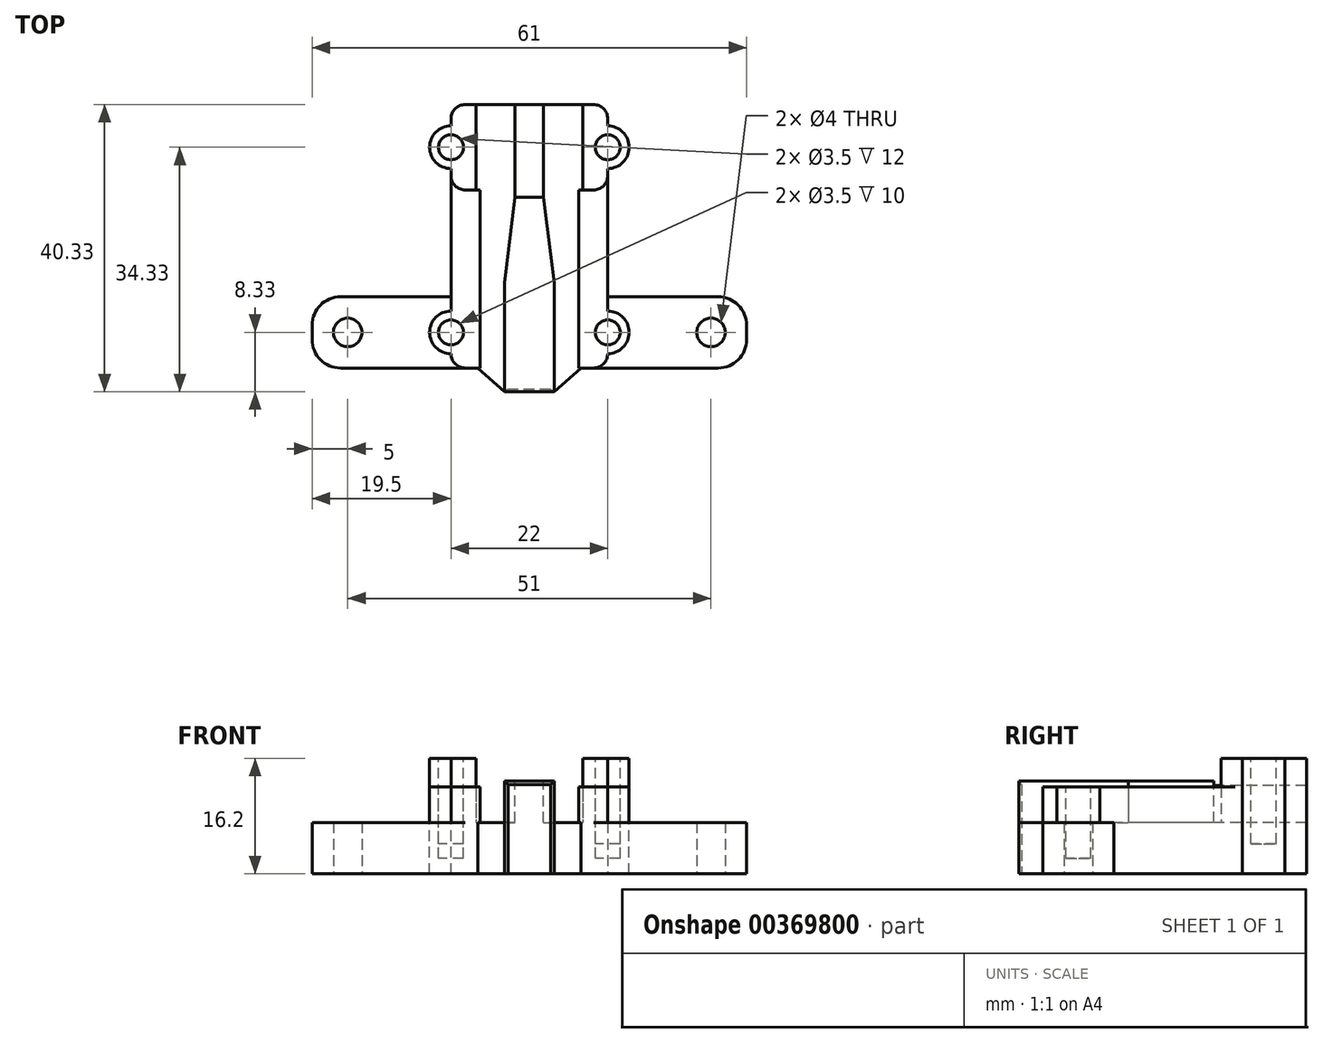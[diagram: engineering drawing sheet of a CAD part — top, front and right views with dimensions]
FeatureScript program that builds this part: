
annotation { "Feature Type Name" : "Feature", "Feature Type Description" : "" }
export const myFeature = defineFeature(function(context is Context, id is Id, definition is map)
    precondition{}
    {
        {
            var Q0;
            Q0=qCreatedBy(makeId("Top.planeOp"),FACE);
            var sketch = newSketch(context, id + "F0", { "sketchPlane" : qUnion([Q0])});
            skLineSegment(sketch, "E0.bottom", {"start": v(0, 0) * mm, "end": v(7, 0) * mm});
            skLineSegment(sketch, "E0.top", {"start": v(0, 15) * mm, "end": v(7, 15) * mm});
            skLineSegment(sketch, "E0.left", {"start": v(0, 0) * mm, "end": v(0, 15) * mm});
            skLineSegment(sketch, "E0.right", {"start": v(7, 0) * mm, "end": v(7, 15) * mm});
            skSolve(sketch);
        }
        {
            var Q0;
            Q0 = qSketchRegion(id + "F0", true);
            extrude(context, id + "F1", {"entities" : qUnion([Q0]), "depth" : 13 * mm});
        }
        {
            var Q0;
            Q0=makeQuery(id+"F1.opExtrude","SWEPT_FACE",FACE,{"disambiguationData":[OSD([sQuery(id+"F0.wireOp",EDGE,"E0.left")])]});
            var sketch = newSketch(context, id + "F2", { "sketchPlane" : qUnion([Q0])});
            skLineSegment(sketch, "E1", {"start": v(0, 13) * mm, "end": v(0.33, 13) * mm});
            skLineSegment(sketch, "E2", {"start": v(0.33, 13) * mm, "end": v(0, 12.5) * mm});
            skLineSegment(sketch, "E3", {"start": v(0, 12.5) * mm, "end": v(0, 13) * mm});
            skSolve(sketch);
        }
        {
            var Q0;
            Q0 = qSketchRegion(id + "F2", true);
            var Q1;
            Q1=makeQuery(id+"F1.opExtrude","SWEPT_FACE",FACE,{"disambiguationData":[OSD([sQuery(id+"F0.wireOp",EDGE,"E0.right")])]});
            extrude(context, id + "F3", {"entities" : qUnion([Q0]), "operationType" : NewBodyOperationType.ADD, "endBound" : BoundingType.UP_TO_SURFACE, "oppositeDirection" : true, "endBoundEntityFace" : qUnion([Q1]), "depth" : 25 * mm});
        }
        {
            var Q0;
            Q0=makeQuery(id+"F1.opExtrude","CAP_FACE",FACE,{"disambiguationData":[OSD([sQuery(id+"F0.wireOp",EDGE,"E0.bottom"),sQuery(id+"F0.wireOp",EDGE,"E0.top"),sQuery(id+"F0.wireOp",EDGE,"E0.left"),sQuery(id+"F0.wireOp",EDGE,"E0.right")])],"isStart":true});
            var sketch = newSketch(context, id + "F4", { "sketchPlane" : qUnion([Q0])});
            skLineSegment(sketch, "E4", {"start": v(0, 0) * mm, "end": v(0, 0.33) * mm});
            skLineSegment(sketch, "E5", {"start": v(0, 0.33) * mm, "end": v(0.5, 0) * mm});
            skLineSegment(sketch, "E6", {"start": v(0.5, 0) * mm, "end": v(0, 0) * mm});
            skLineSegment(sketch, "E7", {"start": v(7, 0) * mm, "end": v(7, 0.33) * mm});
            skLineSegment(sketch, "E8", {"start": v(7, 0.33) * mm, "end": v(6.5, 0) * mm});
            skLineSegment(sketch, "E9", {"start": v(6.5, 0) * mm, "end": v(7, 0) * mm});
            skSolve(sketch);
        }
        {
            var Q0;
            Q0 = qSketchRegion(id + "F4", true);
            var Q1;
            Q1=makeQuery(id+"F3.boolean.opBoolean","MERGE",FACE,{"derivedFrom":[makeQuery(id+"F1.opExtrude","CAP_FACE",FACE,{"disambiguationData":[OSD([sQuery(id+"F0.wireOp",EDGE,"E0.bottom"),sQuery(id+"F0.wireOp",EDGE,"E0.top"),sQuery(id+"F0.wireOp",EDGE,"E0.left"),sQuery(id+"F0.wireOp",EDGE,"E0.right")])],"isStart":false}),makeQuery(id+"F3.opExtrude","SWEPT_FACE",FACE,{"disambiguationData":[OSD([sQuery(id+"F2.wireOp",EDGE,"E1")])]})]});
            extrude(context, id + "F5", {"entities" : qUnion([Q0]), "operationType" : NewBodyOperationType.ADD, "endBound" : BoundingType.UP_TO_SURFACE, "oppositeDirection" : true, "endBoundEntityFace" : qUnion([Q1]), "depth" : 25 * mm});
        }
        {
            var Q0;
            Q0=makeQuery(id+"F5.boolean.opBoolean","MERGE",FACE,{"derivedFrom":[makeQuery(id+"F1.opExtrude","CAP_FACE",FACE,{"disambiguationData":[OSD([sQuery(id+"F0.wireOp",EDGE,"E0.bottom"),sQuery(id+"F0.wireOp",EDGE,"E0.top"),sQuery(id+"F0.wireOp",EDGE,"E0.left"),sQuery(id+"F0.wireOp",EDGE,"E0.right")])],"isStart":true}),makeQuery(id+"F5.opExtrude","CAP_FACE",FACE,{"disambiguationData":[OSD([sQuery(id+"F4.wireOp",EDGE,"E4"),sQuery(id+"F4.wireOp",EDGE,"E5"),sQuery(id+"F4.wireOp",EDGE,"E6")])],"isStart":true}),makeQuery(id+"F5.opExtrude","CAP_FACE",FACE,{"disambiguationData":[OSD([sQuery(id+"F4.wireOp",EDGE,"E7"),sQuery(id+"F4.wireOp",EDGE,"E8"),sQuery(id+"F4.wireOp",EDGE,"E9")])],"isStart":true})]});
            var sketch = newSketch(context, id + "F6", { "sketchPlane" : qUnion([Q0])});
            skLineSegment(sketch, "E10.bottom", {"start": v(0, -3) * mm, "end": v(-23, -3) * mm});
            skLineSegment(sketch, "E10.top", {"start": v(0, -13) * mm, "end": v(-23, -13) * mm});
            skLineSegment(sketch, "E10.left", {"start": v(0, -3) * mm, "end": v(0, -13) * mm});
            skLineSegment(sketch, "E10.right", {"start": v(-27, -7) * mm, "end": v(-27, -9) * mm});
            skLineSegment(sketch, "E11.bottom", {"start": v(7, -3) * mm, "end": v(30, -3) * mm});
            skLineSegment(sketch, "E11.top", {"start": v(7, -13) * mm, "end": v(30, -13) * mm});
            skLineSegment(sketch, "E11.left", {"start": v(7, -3) * mm, "end": v(7, -13) * mm});
            skLineSegment(sketch, "E11.right", {"start": v(34, -7) * mm, "end": v(34, -9) * mm});
            skPoint(sketch, "E12.visualSharp", {"position": v(34, -13) * mm});
            skArc(sketch, "E12.filletArc", {"start": v(30, -13) * mm, "mid": v(32.83, -11.83) * mm, "end": v(34, -9) * mm});
            skPoint(sketch, "E13.visualSharp", {"position": v(34, -3) * mm});
            skArc(sketch, "E13.filletArc", {"start": v(34, -7) * mm, "mid": v(32.83, -4.17) * mm, "end": v(30, -3) * mm});
            skPoint(sketch, "E14.visualSharp", {"position": v(-27, -13) * mm});
            skArc(sketch, "E14.filletArc", {"start": v(-27, -9) * mm, "mid": v(-25.83, -11.83) * mm, "end": v(-23, -13) * mm});
            skPoint(sketch, "E15.visualSharp", {"position": v(-27, -3) * mm});
            skArc(sketch, "E15.filletArc", {"start": v(-23, -3) * mm, "mid": v(-25.83, -4.17) * mm, "end": v(-27, -7) * mm});
            skSolve(sketch);
        }
        {
            var Q0;
            Q0 = qSketchRegion(id + "F6", true);
            extrude(context, id + "F7", {"entities" : qUnion([Q0]), "operationType" : NewBodyOperationType.ADD, "oppositeDirection" : true, "depth" : 7.2 * mm});
        }
        {
            var Q0;
            Q0=makeQuery(id+"F7.boolean.opBoolean","MERGE",FACE,{"derivedFrom":[makeQuery(id+"F5.boolean.opBoolean","MERGE",FACE,{"derivedFrom":[makeQuery(id+"F1.opExtrude","CAP_FACE",FACE,{"disambiguationData":[OSD([sQuery(id+"F0.wireOp",EDGE,"E0.bottom"),sQuery(id+"F0.wireOp",EDGE,"E0.top"),sQuery(id+"F0.wireOp",EDGE,"E0.left"),sQuery(id+"F0.wireOp",EDGE,"E0.right")])],"isStart":true}),makeQuery(id+"F5.opExtrude","CAP_FACE",FACE,{"disambiguationData":[OSD([sQuery(id+"F4.wireOp",EDGE,"E4"),sQuery(id+"F4.wireOp",EDGE,"E5"),sQuery(id+"F4.wireOp",EDGE,"E6")])],"isStart":true}),makeQuery(id+"F5.opExtrude","CAP_FACE",FACE,{"disambiguationData":[OSD([sQuery(id+"F4.wireOp",EDGE,"E7"),sQuery(id+"F4.wireOp",EDGE,"E8"),sQuery(id+"F4.wireOp",EDGE,"E9")])],"isStart":true})]}),makeQuery(id+"F7.opExtrude","CAP_FACE",FACE,{"disambiguationData":[OSD([sQuery(id+"F6.wireOp",EDGE,"E10.bottom"),sQuery(id+"F6.wireOp",EDGE,"E10.top"),sQuery(id+"F6.wireOp",EDGE,"E10.left"),sQuery(id+"F6.wireOp",EDGE,"E10.right")])],"isStart":true}),makeQuery(id+"F7.opExtrude","CAP_FACE",FACE,{"disambiguationData":[OSD([sQuery(id+"F6.wireOp",EDGE,"E11.bottom"),sQuery(id+"F6.wireOp",EDGE,"E11.top"),sQuery(id+"F6.wireOp",EDGE,"E11.left"),sQuery(id+"F6.wireOp",EDGE,"E11.right")])],"isStart":true})]});
            var sketch = newSketch(context, id + "F8", { "sketchPlane" : qUnion([Q0])});
            skCircle(sketch, "E16", {"center": v(-22, -8) * mm, "radius": 2 * mm});
            skCircle(sketch, "E17", {"center": v(29, -8) * mm, "radius": 2 * mm});
            skSolve(sketch);
        }
        {
            var Q0;
            Q0 = qSketchRegion(id + "F8", true);
            extrude(context, id + "F9", {"entities" : qUnion([Q0]), "operationType" : NewBodyOperationType.REMOVE, "oppositeDirection" : true, "depth" : 25 * mm});
        }
        {
            var Q0;
            Q0=makeQuery(id+"F1.opExtrude","SWEPT_FACE",FACE,{"disambiguationData":[OSD([sQuery(id+"F0.wireOp",EDGE,"E0.top")])]});
            var sketch = newSketch(context, id + "F10", { "sketchPlane" : qUnion([Q0])});
            skLineSegment(sketch, "E18.bottom", {"start": v(-5.5, 12.4) * mm, "end": v(-1.5, 12.4) * mm});
            skLineSegment(sketch, "E18.top", {"start": v(-5.5, 0) * mm, "end": v(-1.5, 0) * mm});
            skLineSegment(sketch, "E18.left", {"start": v(-5.5, 12.4) * mm, "end": v(-5.5, 0) * mm});
            skLineSegment(sketch, "E18.right", {"start": v(-1.5, 12.4) * mm, "end": v(-1.5, 0) * mm});
            skSolve(sketch);
        }
        {
            var Q0;
            Q0 = qSketchRegion(id + "F10", true);
            extrude(context, id + "F11", {"entities" : qUnion([Q0]), "operationType" : NewBodyOperationType.ADD, "depth" : 25 * mm});
        }
        {
            var Q0;
            Q0=makeQuery(id+"F11.boolean.opBoolean","MERGE",FACE,{"derivedFrom":[makeQuery(id+"F7.boolean.opBoolean","MERGE",FACE,{"derivedFrom":[makeQuery(id+"F5.boolean.opBoolean","MERGE",FACE,{"derivedFrom":[makeQuery(id+"F1.opExtrude","CAP_FACE",FACE,{"disambiguationData":[OSD([sQuery(id+"F0.wireOp",EDGE,"E0.bottom"),sQuery(id+"F0.wireOp",EDGE,"E0.top"),sQuery(id+"F0.wireOp",EDGE,"E0.left"),sQuery(id+"F0.wireOp",EDGE,"E0.right")])],"isStart":true}),makeQuery(id+"F5.opExtrude","CAP_FACE",FACE,{"disambiguationData":[OSD([sQuery(id+"F4.wireOp",EDGE,"E4"),sQuery(id+"F4.wireOp",EDGE,"E5"),sQuery(id+"F4.wireOp",EDGE,"E6")])],"isStart":true}),makeQuery(id+"F5.opExtrude","CAP_FACE",FACE,{"disambiguationData":[OSD([sQuery(id+"F4.wireOp",EDGE,"E7"),sQuery(id+"F4.wireOp",EDGE,"E8"),sQuery(id+"F4.wireOp",EDGE,"E9")])],"isStart":true})]}),makeQuery(id+"F7.opExtrude","CAP_FACE",FACE,{"disambiguationData":[OSD([sQuery(id+"F6.wireOp",EDGE,"E10.bottom"),sQuery(id+"F6.wireOp",EDGE,"E10.top"),sQuery(id+"F6.wireOp",EDGE,"E10.left"),sQuery(id+"F6.wireOp",EDGE,"E10.right"),sQuery(id+"F6.wireOp",EDGE,"E14.filletArc"),sQuery(id+"F6.wireOp",EDGE,"E15.filletArc")])],"isStart":true}),makeQuery(id+"F7.opExtrude","CAP_FACE",FACE,{"disambiguationData":[OSD([sQuery(id+"F6.wireOp",EDGE,"E11.bottom"),sQuery(id+"F6.wireOp",EDGE,"E11.top"),sQuery(id+"F6.wireOp",EDGE,"E11.left"),sQuery(id+"F6.wireOp",EDGE,"E11.right"),sQuery(id+"F6.wireOp",EDGE,"E12.filletArc"),sQuery(id+"F6.wireOp",EDGE,"E13.filletArc")])],"isStart":true})]}),makeQuery(id+"F11.opExtrude","SWEPT_FACE",FACE,{"disambiguationData":[OSD([sQuery(id+"F10.wireOp",EDGE,"E18.top")])]})]});
            var sketch = newSketch(context, id + "F12", { "sketchPlane" : qUnion([Q0])});
            skLineSegment(sketch, "E19.bottom", {"start": v(-7.5, -15) * mm, "end": v(14.5, -15) * mm});
            skLineSegment(sketch, "E19.top", {"start": v(-7.5, -40) * mm, "end": v(14.5, -40) * mm});
            skLineSegment(sketch, "E19.left", {"start": v(-7.5, -15) * mm, "end": v(-7.5, -40) * mm});
            skLineSegment(sketch, "E19.right", {"start": v(14.5, -15) * mm, "end": v(14.5, -40) * mm});
            skSolve(sketch);
        }
        {
            var Q0;
            Q0 = qSketchRegion(id + "F12", true);
            extrude(context, id + "F13", {"entities" : qUnion([Q0]), "operationType" : NewBodyOperationType.ADD, "oppositeDirection" : true, "depth" : 7.2 * mm});
        }
        {
            var Q0;
            Q0=makeQuery(id+"F7.opExtrude","SWEPT_FACE",FACE,{"disambiguationData":[OSD([sQuery(id+"F6.wireOp",EDGE,"E11.top")])]});
            var sketch = newSketch(context, id + "F14", { "sketchPlane" : qUnion([Q0])});
            skLineSegment(sketch, "E20.bottom", {"start": v(-7, 7.2) * mm, "end": v(-14.5, 7.2) * mm});
            skLineSegment(sketch, "E20.top", {"start": v(-7, 0) * mm, "end": v(-14.5, 0) * mm});
            skLineSegment(sketch, "E20.left", {"start": v(-7, 7.2) * mm, "end": v(-7, 0) * mm});
            skLineSegment(sketch, "E20.right", {"start": v(-14.5, 7.2) * mm, "end": v(-14.5, 0) * mm});
            skLineSegment(sketch, "E21.bottom", {"start": v(0, 0) * mm, "end": v(7.5, 0) * mm});
            skLineSegment(sketch, "E21.top", {"start": v(0, 7.2) * mm, "end": v(7.5, 7.2) * mm});
            skLineSegment(sketch, "E21.left", {"start": v(0, 0) * mm, "end": v(0, 7.2) * mm});
            skLineSegment(sketch, "E21.right", {"start": v(7.5, 0) * mm, "end": v(7.5, 7.2) * mm});
            skSolve(sketch);
        }
        {
            var Q0;
            Q0 = qSketchRegion(id + "F14", true);
            extrude(context, id + "F15", {"entities" : qUnion([Q0]), "operationType" : NewBodyOperationType.ADD, "endBound" : BoundingType.UP_TO_NEXT, "depth" : 25 * mm});
        }
        {
            var Q0;
            Q0=makeQuery(id+"F11.opExtrude","SWEPT_FACE",FACE,{"disambiguationData":[OSD([sQuery(id+"F10.wireOp",EDGE,"E18.bottom")])]});
            var sketch = newSketch(context, id + "F16", { "sketchPlane" : qUnion([Q0])});
            skLineSegment(sketch, "E22.bottom", {"start": v(7, 15) * mm, "end": v(0, 15) * mm});
            skLineSegment(sketch, "E22.top", {"start": v(5.5, 27) * mm, "end": v(1.5, 27) * mm});
            skLineSegment(sketch, "E23", {"start": v(7, 15) * mm, "end": v(5.5, 27) * mm});
            skLineSegment(sketch, "E24", {"start": v(0, 15) * mm, "end": v(1.5, 27) * mm});
            skPoint(sketch, "E22.right.end.orphan", {"position": v(0, 27) * mm});
            skSolve(sketch);
        }
        {
            var Q0;
            Q0 = qSketchRegion(id + "F16", true);
            extrude(context, id + "F17", {"entities" : qUnion([Q0]), "operationType" : NewBodyOperationType.ADD, "oppositeDirection" : true, "depth" : 6 * mm, "hasSecondDirection" : true, "secondDirectionOppositeDirection" : false, "secondDirectionDepth" : .6 * mm});
        }
        {
            var Q0;
            {var subQ1=sQuery(id+"F12.wireOp",EDGE,"E19.bottom");var subQ2=sQuery(id+"F12.wireOp",EDGE,"E19.top");var subQ3=sQuery(id+"F12.wireOp",EDGE,"E19.left");Q0=makeQuery(id+"F13.boolean.opBoolean","SPLIT",FACE,{"disambiguationData":[TD([makeQuery(id+"F1.opExtrude","SWEPT_FACE",FACE,{"disambiguationData":[OSD([sQuery(id+"F0.wireOp",EDGE,"E0.left")])]})])],"derivedFrom":makeQuery(id+"F13.opExtrude","CAP_FACE",FACE,{"disambiguationData":[OSD([subQ1,subQ2,subQ3,sQuery(id+"F12.wireOp",EDGE,"E19.right")])],"isStart":false})});}
            var sketch = newSketch(context, id + "F18", { "sketchPlane" : qUnion([Q0])});
            skLineSegment(sketch, "E25.bottom", {"start": v(-7.5, 40) * mm, "end": v(-4, 40) * mm});
            skLineSegment(sketch, "E25.top", {"start": v(-7.5, 28) * mm, "end": v(-4, 28) * mm});
            skLineSegment(sketch, "E25.left", {"start": v(-7.5, 40) * mm, "end": v(-7.5, 28) * mm});
            skLineSegment(sketch, "E25.right", {"start": v(-4, 40) * mm, "end": v(-4, 28) * mm});
            skSolve(sketch);
        }
        {
            var Q0;
            Q0 = qSketchRegion(id + "F18", true);
            extrude(context, id + "F19", {"entities" : qUnion([Q0]), "operationType" : NewBodyOperationType.ADD, "depth" : 9 * mm});
        }
        {
            var Q0;
            {var subQ0=sQuery(id+"F0.wireOp",EDGE,"E0.right");var subQ2=sQuery(id+"F12.wireOp",EDGE,"E19.bottom");var subQ3=sQuery(id+"F12.wireOp",EDGE,"E19.top");var subQ4=sQuery(id+"F12.wireOp",EDGE,"E19.right");Q0=makeQuery(id+"F13.boolean.opBoolean","SPLIT",FACE,{"disambiguationData":[TD([makeQuery(id+"F1.opExtrude","SWEPT_FACE",FACE,{"disambiguationData":[OSD([subQ0])]})])],"derivedFrom":makeQuery(id+"F13.opExtrude","CAP_FACE",FACE,{"disambiguationData":[OSD([subQ2,subQ3,sQuery(id+"F12.wireOp",EDGE,"E19.left"),subQ4])],"isStart":false})});}
            var sketch = newSketch(context, id + "F20", { "sketchPlane" : qUnion([Q0])});
            skLineSegment(sketch, "E26.bottom", {"start": v(14.5, 40) * mm, "end": v(11, 40) * mm});
            skLineSegment(sketch, "E26.top", {"start": v(14.5, 28) * mm, "end": v(11, 28) * mm});
            skLineSegment(sketch, "E26.left", {"start": v(14.5, 40) * mm, "end": v(14.5, 28) * mm});
            skLineSegment(sketch, "E26.right", {"start": v(11, 40) * mm, "end": v(11, 28) * mm});
            skSolve(sketch);
        }
        {
            var Q0;
            Q0 = qSketchRegion(id + "F20", true);
            extrude(context, id + "F21", {"entities" : qUnion([Q0]), "operationType" : NewBodyOperationType.ADD, "depth" : 9 * mm});
        }
        {
            var Q0;
            Q0=makeQuery(id+"F21.opExtrude","CAP_FACE",FACE,{"disambiguationData":[OSD([sQuery(id+"F20.wireOp",EDGE,"E26.bottom"),sQuery(id+"F20.wireOp",EDGE,"E26.top"),sQuery(id+"F20.wireOp",EDGE,"E26.left"),sQuery(id+"F20.wireOp",EDGE,"E26.right")])],"isStart":false});
            var sketch = newSketch(context, id + "F22", { "sketchPlane" : qUnion([Q0])});
            skCircle(sketch, "E27", {"center": v(14.5, 34) * mm, "radius": 3 * mm});
            skSolve(sketch);
        }
        {
            var Q0;
            Q0 = qSketchRegion(id + "F22", true);
            var Q1;
            Q1=makeQuery(id+"F15.boolean.opBoolean","MERGE",FACE,{"derivedFrom":[makeQuery(id+"F13.boolean.opBoolean","MERGE",FACE,{"derivedFrom":[makeQuery(id+"F11.boolean.opBoolean","MERGE",FACE,{"derivedFrom":[makeQuery(id+"F7.boolean.opBoolean","MERGE",FACE,{"derivedFrom":[makeQuery(id+"F5.boolean.opBoolean","MERGE",FACE,{"derivedFrom":[makeQuery(id+"F1.opExtrude","CAP_FACE",FACE,{"disambiguationData":[OSD([sQuery(id+"F0.wireOp",EDGE,"E0.bottom"),sQuery(id+"F0.wireOp",EDGE,"E0.top"),sQuery(id+"F0.wireOp",EDGE,"E0.left"),sQuery(id+"F0.wireOp",EDGE,"E0.right")])],"isStart":true}),makeQuery(id+"F5.opExtrude","CAP_FACE",FACE,{"disambiguationData":[OSD([sQuery(id+"F4.wireOp",EDGE,"E4"),sQuery(id+"F4.wireOp",EDGE,"E5"),sQuery(id+"F4.wireOp",EDGE,"E6")])],"isStart":true}),makeQuery(id+"F5.opExtrude","CAP_FACE",FACE,{"disambiguationData":[OSD([sQuery(id+"F4.wireOp",EDGE,"E7"),sQuery(id+"F4.wireOp",EDGE,"E8"),sQuery(id+"F4.wireOp",EDGE,"E9")])],"isStart":true})]}),makeQuery(id+"F7.opExtrude","CAP_FACE",FACE,{"disambiguationData":[OSD([sQuery(id+"F6.wireOp",EDGE,"E10.bottom"),sQuery(id+"F6.wireOp",EDGE,"E10.top"),sQuery(id+"F6.wireOp",EDGE,"E10.left"),sQuery(id+"F6.wireOp",EDGE,"E10.right"),sQuery(id+"F6.wireOp",EDGE,"E14.filletArc"),sQuery(id+"F6.wireOp",EDGE,"E15.filletArc")])],"isStart":true}),makeQuery(id+"F7.opExtrude","CAP_FACE",FACE,{"disambiguationData":[OSD([sQuery(id+"F6.wireOp",EDGE,"E11.bottom"),sQuery(id+"F6.wireOp",EDGE,"E11.top"),sQuery(id+"F6.wireOp",EDGE,"E11.left"),sQuery(id+"F6.wireOp",EDGE,"E11.right"),sQuery(id+"F6.wireOp",EDGE,"E12.filletArc"),sQuery(id+"F6.wireOp",EDGE,"E13.filletArc")])],"isStart":true})]}),makeQuery(id+"F11.opExtrude","SWEPT_FACE",FACE,{"disambiguationData":[OSD([sQuery(id+"F10.wireOp",EDGE,"E18.top")])]})]}),makeQuery(id+"F13.opExtrude","CAP_FACE",FACE,{"disambiguationData":[OSD([sQuery(id+"F12.wireOp",EDGE,"E19.bottom"),sQuery(id+"F12.wireOp",EDGE,"E19.top"),sQuery(id+"F12.wireOp",EDGE,"E19.left"),sQuery(id+"F12.wireOp",EDGE,"E19.right")])],"isStart":true})]}),makeQuery(id+"F15.opExtrude","SWEPT_FACE",FACE,{"disambiguationData":[OSD([sQuery(id+"F14.wireOp",EDGE,"E20.top")])]}),makeQuery(id+"F15.opExtrude","SWEPT_FACE",FACE,{"disambiguationData":[OSD([sQuery(id+"F14.wireOp",EDGE,"E21.bottom")])]})]});
            extrude(context, id + "F23", {"entities" : qUnion([Q0]), "operationType" : NewBodyOperationType.ADD, "endBound" : BoundingType.UP_TO_SURFACE, "oppositeDirection" : true, "endBoundEntityFace" : qUnion([Q1]), "depth" : 25 * mm});
        }
        {
            var Q0;
            Q0=makeQuery(id+"F19.opExtrude","CAP_FACE",FACE,{"disambiguationData":[OSD([sQuery(id+"F18.wireOp",EDGE,"E25.bottom"),sQuery(id+"F18.wireOp",EDGE,"E25.top"),sQuery(id+"F18.wireOp",EDGE,"E25.left"),sQuery(id+"F18.wireOp",EDGE,"E25.right")])],"isStart":false});
            var sketch = newSketch(context, id + "F24", { "sketchPlane" : qUnion([Q0])});
            skCircle(sketch, "E28", {"center": v(-7.5, 34) * mm, "radius": 3 * mm});
            skSolve(sketch);
        }
        {
            var Q0;
            Q0 = qSketchRegion(id + "F24", true);
            var Q1;
            Q1=makeQuery(id+"F23.boolean.opBoolean","MERGE",FACE,{"derivedFrom":[makeQuery(id+"F15.boolean.opBoolean","MERGE",FACE,{"derivedFrom":[makeQuery(id+"F13.boolean.opBoolean","MERGE",FACE,{"derivedFrom":[makeQuery(id+"F11.boolean.opBoolean","MERGE",FACE,{"derivedFrom":[makeQuery(id+"F7.boolean.opBoolean","MERGE",FACE,{"derivedFrom":[makeQuery(id+"F5.boolean.opBoolean","MERGE",FACE,{"derivedFrom":[makeQuery(id+"F1.opExtrude","CAP_FACE",FACE,{"disambiguationData":[OSD([sQuery(id+"F0.wireOp",EDGE,"E0.bottom"),sQuery(id+"F0.wireOp",EDGE,"E0.top"),sQuery(id+"F0.wireOp",EDGE,"E0.left"),sQuery(id+"F0.wireOp",EDGE,"E0.right")])],"isStart":true}),makeQuery(id+"F5.opExtrude","CAP_FACE",FACE,{"disambiguationData":[OSD([sQuery(id+"F4.wireOp",EDGE,"E4"),sQuery(id+"F4.wireOp",EDGE,"E5"),sQuery(id+"F4.wireOp",EDGE,"E6")])],"isStart":true}),makeQuery(id+"F5.opExtrude","CAP_FACE",FACE,{"disambiguationData":[OSD([sQuery(id+"F4.wireOp",EDGE,"E7"),sQuery(id+"F4.wireOp",EDGE,"E8"),sQuery(id+"F4.wireOp",EDGE,"E9")])],"isStart":true})]}),makeQuery(id+"F7.opExtrude","CAP_FACE",FACE,{"disambiguationData":[OSD([sQuery(id+"F6.wireOp",EDGE,"E10.bottom"),sQuery(id+"F6.wireOp",EDGE,"E10.top"),sQuery(id+"F6.wireOp",EDGE,"E10.left"),sQuery(id+"F6.wireOp",EDGE,"E10.right"),sQuery(id+"F6.wireOp",EDGE,"E14.filletArc"),sQuery(id+"F6.wireOp",EDGE,"E15.filletArc")])],"isStart":true}),makeQuery(id+"F7.opExtrude","CAP_FACE",FACE,{"disambiguationData":[OSD([sQuery(id+"F6.wireOp",EDGE,"E11.bottom"),sQuery(id+"F6.wireOp",EDGE,"E11.top"),sQuery(id+"F6.wireOp",EDGE,"E11.left"),sQuery(id+"F6.wireOp",EDGE,"E11.right"),sQuery(id+"F6.wireOp",EDGE,"E12.filletArc"),sQuery(id+"F6.wireOp",EDGE,"E13.filletArc")])],"isStart":true})]}),makeQuery(id+"F11.opExtrude","SWEPT_FACE",FACE,{"disambiguationData":[OSD([sQuery(id+"F10.wireOp",EDGE,"E18.top")])]})]}),makeQuery(id+"F13.opExtrude","CAP_FACE",FACE,{"disambiguationData":[OSD([sQuery(id+"F12.wireOp",EDGE,"E19.bottom"),sQuery(id+"F12.wireOp",EDGE,"E19.top"),sQuery(id+"F12.wireOp",EDGE,"E19.left"),sQuery(id+"F12.wireOp",EDGE,"E19.right")])],"isStart":true})]}),makeQuery(id+"F15.opExtrude","SWEPT_FACE",FACE,{"disambiguationData":[OSD([sQuery(id+"F14.wireOp",EDGE,"E20.top")])]}),makeQuery(id+"F15.opExtrude","SWEPT_FACE",FACE,{"disambiguationData":[OSD([sQuery(id+"F14.wireOp",EDGE,"E21.bottom")])]})]}),makeQuery(id+"F23.opExtrude","CAP_FACE",FACE,{"disambiguationData":[OSD([sQuery(id+"F22.wireOp",EDGE,"E27")])],"isStart":false})]});
            extrude(context, id + "F25", {"entities" : qUnion([Q0]), "operationType" : NewBodyOperationType.ADD, "endBound" : BoundingType.UP_TO_SURFACE, "oppositeDirection" : true, "endBoundEntityFace" : qUnion([Q1]), "depth" : 25 * mm});
        }
        {
            var Q0;
            Q0=makeQuery(id+"F25.boolean.opBoolean","MERGE",FACE,{"derivedFrom":[makeQuery(id+"F19.opExtrude","CAP_FACE",FACE,{"disambiguationData":[OSD([sQuery(id+"F18.wireOp",EDGE,"E25.bottom"),sQuery(id+"F18.wireOp",EDGE,"E25.top"),sQuery(id+"F18.wireOp",EDGE,"E25.left"),sQuery(id+"F18.wireOp",EDGE,"E25.right")])],"isStart":false}),makeQuery(id+"F25.opExtrude","CAP_FACE",FACE,{"disambiguationData":[OSD([sQuery(id+"F24.wireOp",EDGE,"E28")])],"isStart":true})]});
            var sketch = newSketch(context, id + "F26", { "sketchPlane" : qUnion([Q0])});
            skCircle(sketch, "E29", {"center": v(-7.5, 34) * mm, "radius": 1.75 * mm});
            skSolve(sketch);
        }
        {
            var Q0;
            Q0 = qSketchRegion(id + "F26", true);
            extrude(context, id + "F27", {"entities" : qUnion([Q0]), "operationType" : NewBodyOperationType.REMOVE, "oppositeDirection" : true, "depth" : 12 * mm});
        }
        {
            var Q0;
            Q0=makeQuery(id+"F23.boolean.opBoolean","MERGE",FACE,{"derivedFrom":[makeQuery(id+"F21.opExtrude","CAP_FACE",FACE,{"disambiguationData":[OSD([sQuery(id+"F20.wireOp",EDGE,"E26.bottom"),sQuery(id+"F20.wireOp",EDGE,"E26.top"),sQuery(id+"F20.wireOp",EDGE,"E26.left"),sQuery(id+"F20.wireOp",EDGE,"E26.right")])],"isStart":false}),makeQuery(id+"F23.opExtrude","CAP_FACE",FACE,{"disambiguationData":[OSD([sQuery(id+"F22.wireOp",EDGE,"E27")])],"isStart":true})]});
            var sketch = newSketch(context, id + "F28", { "sketchPlane" : qUnion([Q0])});
            skCircle(sketch, "E30", {"center": v(14.5, 34) * mm, "radius": 1.75 * mm});
            skSolve(sketch);
        }
        {
            var Q0;
            Q0 = qSketchRegion(id + "F28", true);
            extrude(context, id + "F29", {"entities" : qUnion([Q0]), "operationType" : NewBodyOperationType.REMOVE, "oppositeDirection" : true, "depth" : 12 * mm});
        }
        {
            var Q0;
            {var subQ1=sQuery(id+"F12.wireOp",EDGE,"E19.bottom");var subQ2=sQuery(id+"F12.wireOp",EDGE,"E19.top");var subQ3=sQuery(id+"F12.wireOp",EDGE,"E19.left");Q0=makeQuery(id+"F15.boolean.opBoolean","MERGE",FACE,{"derivedFrom":[makeQuery(id+"F7.opExtrude","CAP_FACE",FACE,{"disambiguationData":[OSD([sQuery(id+"F6.wireOp",EDGE,"E10.bottom"),sQuery(id+"F6.wireOp",EDGE,"E10.top"),sQuery(id+"F6.wireOp",EDGE,"E10.left"),sQuery(id+"F6.wireOp",EDGE,"E10.right"),sQuery(id+"F6.wireOp",EDGE,"E14.filletArc"),sQuery(id+"F6.wireOp",EDGE,"E15.filletArc")])],"isStart":false}),makeQuery(id+"F13.boolean.opBoolean","SPLIT",FACE,{"disambiguationData":[TD([makeQuery(id+"F1.opExtrude","SWEPT_FACE",FACE,{"disambiguationData":[OSD([sQuery(id+"F0.wireOp",EDGE,"E0.left")])]})])],"derivedFrom":makeQuery(id+"F13.opExtrude","CAP_FACE",FACE,{"disambiguationData":[OSD([subQ1,subQ2,subQ3,sQuery(id+"F12.wireOp",EDGE,"E19.right")])],"isStart":false})}),makeQuery(id+"F15.opExtrude","SWEPT_FACE",FACE,{"disambiguationData":[OSD([sQuery(id+"F14.wireOp",EDGE,"E21.top")])]})]});}
            var sketch = newSketch(context, id + "F30", { "sketchPlane" : qUnion([Q0])});
            skLineSegment(sketch, "E31.bottom", {"start": v(-7.5, 28) * mm, "end": v(-3.4, 28) * mm});
            skLineSegment(sketch, "E31.top", {"start": v(-7.5, 3) * mm, "end": v(-3.4, 3) * mm});
            skLineSegment(sketch, "E31.left", {"start": v(-7.5, 28) * mm, "end": v(-7.5, 3) * mm});
            skLineSegment(sketch, "E31.right", {"start": v(-3.4, 28) * mm, "end": v(-3.4, 3) * mm});
            skSolve(sketch);
        }
        {
            var Q0;
            Q0 = qSketchRegion(id + "F30", true);
            extrude(context, id + "F31", {"entities" : qUnion([Q0]), "operationType" : NewBodyOperationType.ADD, "depth" : 5 * mm});
        }
        {
            var Q0;
            {var subQ1=sQuery(id+"F12.wireOp",EDGE,"E19.bottom");var subQ2=sQuery(id+"F12.wireOp",EDGE,"E19.top");var subQ3=sQuery(id+"F12.wireOp",EDGE,"E19.right");Q0=makeQuery(id+"F15.boolean.opBoolean","MERGE",FACE,{"derivedFrom":[makeQuery(id+"F7.opExtrude","CAP_FACE",FACE,{"disambiguationData":[OSD([sQuery(id+"F6.wireOp",EDGE,"E11.bottom"),sQuery(id+"F6.wireOp",EDGE,"E11.top"),sQuery(id+"F6.wireOp",EDGE,"E11.left"),sQuery(id+"F6.wireOp",EDGE,"E11.right"),sQuery(id+"F6.wireOp",EDGE,"E12.filletArc"),sQuery(id+"F6.wireOp",EDGE,"E13.filletArc")])],"isStart":false}),makeQuery(id+"F13.boolean.opBoolean","SPLIT",FACE,{"disambiguationData":[TD([makeQuery(id+"F1.opExtrude","SWEPT_FACE",FACE,{"disambiguationData":[OSD([sQuery(id+"F0.wireOp",EDGE,"E0.right")])]})])],"derivedFrom":makeQuery(id+"F13.opExtrude","CAP_FACE",FACE,{"disambiguationData":[OSD([subQ1,subQ2,sQuery(id+"F12.wireOp",EDGE,"E19.left"),subQ3])],"isStart":false})}),makeQuery(id+"F15.opExtrude","SWEPT_FACE",FACE,{"disambiguationData":[OSD([sQuery(id+"F14.wireOp",EDGE,"E20.bottom")])]})]});}
            var sketch = newSketch(context, id + "F32", { "sketchPlane" : qUnion([Q0])});
            skLineSegment(sketch, "E32.bottom", {"start": v(14.5, 28) * mm, "end": v(10.4, 28) * mm});
            skLineSegment(sketch, "E32.top", {"start": v(14.5, 3) * mm, "end": v(10.4, 3) * mm});
            skLineSegment(sketch, "E32.left", {"start": v(14.5, 28) * mm, "end": v(14.5, 3) * mm});
            skLineSegment(sketch, "E32.right", {"start": v(10.4, 28) * mm, "end": v(10.4, 3) * mm});
            skSolve(sketch);
        }
        {
            var Q0;
            Q0 = qSketchRegion(id + "F32", true);
            extrude(context, id + "F33", {"entities" : qUnion([Q0]), "operationType" : NewBodyOperationType.ADD, "depth" : 5 * mm});
        }
        {
            var Q0;
            Q0=makeQuery(id+"F31.opExtrude","CAP_FACE",FACE,{"disambiguationData":[OSD([sQuery(id+"F30.wireOp",EDGE,"E31.bottom"),sQuery(id+"F30.wireOp",EDGE,"E31.top"),sQuery(id+"F30.wireOp",EDGE,"E31.left"),sQuery(id+"F30.wireOp",EDGE,"E31.right")])],"isStart":false});
            var sketch = newSketch(context, id + "F34", { "sketchPlane" : qUnion([Q0])});
            skCircle(sketch, "E33", {"center": v(-7.5, 8) * mm, "radius": 3 * mm});
            skSolve(sketch);
        }
        {
            var Q0;
            Q0 = qSketchRegion(id + "F34", true);
            var Q1;
            {var subQ0=sQuery(id+"F12.wireOp",EDGE,"E19.left");var subQ2=sQuery(id+"F6.wireOp",EDGE,"E15.filletArc");var subQ3=sQuery(id+"F6.wireOp",EDGE,"E10.bottom");var subQ4=sQuery(id+"F6.wireOp",EDGE,"E10.right");var subQ5=sQuery(id+"F6.wireOp",EDGE,"E10.top");var subQ6=sQuery(id+"F6.wireOp",EDGE,"E14.filletArc");var subQ8=sQuery(id+"F12.wireOp",EDGE,"E19.bottom");var subQ9=sQuery(id+"F12.wireOp",EDGE,"E19.top");Q1=makeQuery(id+"F31.boolean.opBoolean","SPLIT",FACE,{"disambiguationData":[TD([makeQuery(id+"F7.opExtrude","SWEPT_FACE",FACE,{"disambiguationData":[OSD([subQ5])]})])],"derivedFrom":makeQuery(id+"F15.boolean.opBoolean","MERGE",FACE,{"derivedFrom":[makeQuery(id+"F7.opExtrude","CAP_FACE",FACE,{"disambiguationData":[OSD([subQ3,subQ5,sQuery(id+"F6.wireOp",EDGE,"E10.left"),subQ4,subQ6,subQ2])],"isStart":false}),makeQuery(id+"F13.boolean.opBoolean","SPLIT",FACE,{"disambiguationData":[TD([makeQuery(id+"F1.opExtrude","SWEPT_FACE",FACE,{"disambiguationData":[OSD([sQuery(id+"F0.wireOp",EDGE,"E0.left")])]})])],"derivedFrom":makeQuery(id+"F13.opExtrude","CAP_FACE",FACE,{"disambiguationData":[OSD([subQ8,subQ9,subQ0,sQuery(id+"F12.wireOp",EDGE,"E19.right")])],"isStart":false})}),makeQuery(id+"F15.opExtrude","SWEPT_FACE",FACE,{"disambiguationData":[OSD([sQuery(id+"F14.wireOp",EDGE,"E21.top")])]})]})});}
            extrude(context, id + "F35", {"entities" : qUnion([Q0]), "operationType" : NewBodyOperationType.ADD, "endBound" : BoundingType.UP_TO_SURFACE, "oppositeDirection" : true, "endBoundEntityFace" : qUnion([Q1]), "depth" : 25 * mm});
        }
        {
            var Q0;
            Q0=makeQuery(id+"F33.opExtrude","CAP_FACE",FACE,{"disambiguationData":[OSD([sQuery(id+"F32.wireOp",EDGE,"E32.bottom"),sQuery(id+"F32.wireOp",EDGE,"E32.top"),sQuery(id+"F32.wireOp",EDGE,"E32.left"),sQuery(id+"F32.wireOp",EDGE,"E32.right")])],"isStart":false});
            var sketch = newSketch(context, id + "F36", { "sketchPlane" : qUnion([Q0])});
            skCircle(sketch, "E34", {"center": v(14.5, 8) * mm, "radius": 3 * mm});
            skSolve(sketch);
        }
        {
            var Q0;
            Q0 = qSketchRegion(id + "F36", true);
            var Q1;
            {var subQ0=sQuery(id+"F6.wireOp",EDGE,"E11.right");var subQ1=sQuery(id+"F6.wireOp",EDGE,"E13.filletArc");var subQ2=sQuery(id+"F6.wireOp",EDGE,"E11.bottom");var subQ3=sQuery(id+"F12.wireOp",EDGE,"E19.right");var subQ5=sQuery(id+"F6.wireOp",EDGE,"E11.top");var subQ6=sQuery(id+"F6.wireOp",EDGE,"E12.filletArc");var subQ8=sQuery(id+"F12.wireOp",EDGE,"E19.bottom");var subQ9=sQuery(id+"F12.wireOp",EDGE,"E19.top");Q1=makeQuery(id+"F33.boolean.opBoolean","SPLIT",FACE,{"disambiguationData":[TD([makeQuery(id+"F7.opExtrude","SWEPT_FACE",FACE,{"disambiguationData":[OSD([subQ5])]})])],"derivedFrom":makeQuery(id+"F15.boolean.opBoolean","MERGE",FACE,{"derivedFrom":[makeQuery(id+"F7.opExtrude","CAP_FACE",FACE,{"disambiguationData":[OSD([subQ2,subQ5,sQuery(id+"F6.wireOp",EDGE,"E11.left"),subQ0,subQ6,subQ1])],"isStart":false}),makeQuery(id+"F13.boolean.opBoolean","SPLIT",FACE,{"disambiguationData":[TD([makeQuery(id+"F1.opExtrude","SWEPT_FACE",FACE,{"disambiguationData":[OSD([sQuery(id+"F0.wireOp",EDGE,"E0.right")])]})])],"derivedFrom":makeQuery(id+"F13.opExtrude","CAP_FACE",FACE,{"disambiguationData":[OSD([subQ8,subQ9,sQuery(id+"F12.wireOp",EDGE,"E19.left"),subQ3])],"isStart":false})}),makeQuery(id+"F15.opExtrude","SWEPT_FACE",FACE,{"disambiguationData":[OSD([sQuery(id+"F14.wireOp",EDGE,"E20.bottom")])]})]})});}
            extrude(context, id + "F37", {"entities" : qUnion([Q0]), "operationType" : NewBodyOperationType.ADD, "endBound" : BoundingType.UP_TO_SURFACE, "oppositeDirection" : true, "endBoundEntityFace" : qUnion([Q1]), "depth" : 25 * mm});
        }
        {
            var Q0;
            Q0=makeQuery(id+"F35.boolean.opBoolean","MERGE",FACE,{"derivedFrom":[makeQuery(id+"F31.opExtrude","CAP_FACE",FACE,{"disambiguationData":[OSD([sQuery(id+"F30.wireOp",EDGE,"E31.bottom"),sQuery(id+"F30.wireOp",EDGE,"E31.top"),sQuery(id+"F30.wireOp",EDGE,"E31.left"),sQuery(id+"F30.wireOp",EDGE,"E31.right")])],"isStart":false}),makeQuery(id+"F35.opExtrude","CAP_FACE",FACE,{"disambiguationData":[OSD([sQuery(id+"F34.wireOp",EDGE,"E33")])],"isStart":true})]});
            var sketch = newSketch(context, id + "F38", { "sketchPlane" : qUnion([Q0])});
            skCircle(sketch, "E35", {"center": v(-7.5, 8) * mm, "radius": 1.75 * mm});
            skSolve(sketch);
        }
        {
            var Q0;
            Q0 = qSketchRegion(id + "F38", true);
            extrude(context, id + "F39", {"entities" : qUnion([Q0]), "operationType" : NewBodyOperationType.REMOVE, "oppositeDirection" : true, "depth" : 10 * mm});
        }
        {
            var Q0;
            Q0=makeQuery(id+"F37.boolean.opBoolean","MERGE",FACE,{"derivedFrom":[makeQuery(id+"F33.opExtrude","CAP_FACE",FACE,{"disambiguationData":[OSD([sQuery(id+"F32.wireOp",EDGE,"E32.bottom"),sQuery(id+"F32.wireOp",EDGE,"E32.top"),sQuery(id+"F32.wireOp",EDGE,"E32.left"),sQuery(id+"F32.wireOp",EDGE,"E32.right")])],"isStart":false}),makeQuery(id+"F37.opExtrude","CAP_FACE",FACE,{"disambiguationData":[OSD([sQuery(id+"F36.wireOp",EDGE,"E34")])],"isStart":true})]});
            var sketch = newSketch(context, id + "F40", { "sketchPlane" : qUnion([Q0])});
            skCircle(sketch, "E36", {"center": v(14.5, 8) * mm, "radius": 1.75 * mm});
            skSolve(sketch);
        }
        {
            var Q0;
            Q0 = qSketchRegion(id + "F40", true);
            extrude(context, id + "F41", {"entities" : qUnion([Q0]), "operationType" : NewBodyOperationType.REMOVE, "oppositeDirection" : true, "depth" : 10 * mm});
        }
        {
            var Q0;
            Q0=makeQuery(id+"F21.boolean.opBoolean","MERGE",EDGE,{"derivedFrom":[makeQuery(id+"F13.opExtrude","SWEPT_EDGE",EDGE,{"disambiguationData":[OSD([sQuery(id+"F12.wireOp",EDGE,"E19.top"),sQuery(id+"F12.wireOp",EDGE,"E19.right")])]}),makeQuery(id+"F21.opExtrude","SWEPT_EDGE",EDGE,{"disambiguationData":[OSD([sQuery(id+"F20.wireOp",EDGE,"E26.bottom"),sQuery(id+"F20.wireOp",EDGE,"E26.left")])]})]});
            var Q1;
            Q1=makeQuery(id+"F19.boolean.opBoolean","MERGE",EDGE,{"derivedFrom":[makeQuery(id+"F13.opExtrude","SWEPT_EDGE",EDGE,{"disambiguationData":[OSD([sQuery(id+"F12.wireOp",EDGE,"E19.top"),sQuery(id+"F12.wireOp",EDGE,"E19.left")])]}),makeQuery(id+"F19.opExtrude","SWEPT_EDGE",EDGE,{"disambiguationData":[OSD([sQuery(id+"F18.wireOp",EDGE,"E25.bottom"),sQuery(id+"F18.wireOp",EDGE,"E25.left")])]})]});
            var Q2;
            Q2=makeQuery(id+"F31.opExtrude","SWEPT_EDGE",EDGE,{"disambiguationData":[OSD([sQuery(id+"F6.wireOp",EDGE,"E10.bottom"),sQuery(id+"F30.wireOp",EDGE,"E31.top"),sQuery(id+"F30.wireOp",EDGE,"E31.left")])]});
            var Q3;
            Q3=makeQuery(id+"F33.opExtrude","SWEPT_EDGE",EDGE,{"disambiguationData":[OSD([sQuery(id+"F6.wireOp",EDGE,"E11.bottom"),sQuery(id+"F32.wireOp",EDGE,"E32.top"),sQuery(id+"F32.wireOp",EDGE,"E32.left")])]});
            var Q4;
            Q4=makeQuery(id+"F21.opExtrude","SWEPT_EDGE",EDGE,{"disambiguationData":[OSD([sQuery(id+"F6.wireOp",EDGE,"E11.top"),sQuery(id+"F12.wireOp",EDGE,"E19.right"),sQuery(id+"F14.wireOp",EDGE,"E20.bottom"),sQuery(id+"F14.wireOp",EDGE,"E20.right"),sQuery(id+"F20.wireOp",EDGE,"E26.top"),sQuery(id+"F20.wireOp",EDGE,"E26.left")])]});
            var Q5;
            Q5=makeQuery(id+"F19.opExtrude","SWEPT_EDGE",EDGE,{"disambiguationData":[OSD([sQuery(id+"F12.wireOp",EDGE,"E19.left"),sQuery(id+"F14.wireOp",EDGE,"E21.top"),sQuery(id+"F14.wireOp",EDGE,"E21.right"),sQuery(id+"F18.wireOp",EDGE,"E25.top"),sQuery(id+"F18.wireOp",EDGE,"E25.left")])]});
            var Q6;
            Q6=makeQuery(id+"F15.opExtrude","CAP_EDGE",EDGE,{"disambiguationData":[OSD([sQuery(id+"F14.wireOp",EDGE,"E20.right")])],"isStart":true});
            var Q7;
            Q7=makeQuery(id+"F15.opExtrude","CAP_EDGE",EDGE,{"disambiguationData":[OSD([sQuery(id+"F14.wireOp",EDGE,"E21.right")])],"isStart":true});
            fillet(context, id + "F42", {"entities" : qUnion([Q0, Q1, Q2, Q3, Q4, Q5, Q6, Q7]), "radius" : 2 * mm, "tangentPropagation" : true, "allowEdgeOverflow" : false});
        }
        {
            var Q0;
            Q0=makeQuery(id+"F25.boolean.opBoolean","MERGE",FACE,{"derivedFrom":[makeQuery(id+"F23.boolean.opBoolean","MERGE",FACE,{"derivedFrom":[makeQuery(id+"F15.boolean.opBoolean","MERGE",FACE,{"derivedFrom":[makeQuery(id+"F13.boolean.opBoolean","MERGE",FACE,{"derivedFrom":[makeQuery(id+"F11.boolean.opBoolean","MERGE",FACE,{"derivedFrom":[makeQuery(id+"F7.boolean.opBoolean","MERGE",FACE,{"derivedFrom":[makeQuery(id+"F5.boolean.opBoolean","MERGE",FACE,{"derivedFrom":[makeQuery(id+"F1.opExtrude","CAP_FACE",FACE,{"disambiguationData":[OSD([sQuery(id+"F0.wireOp",EDGE,"E0.bottom"),sQuery(id+"F0.wireOp",EDGE,"E0.top"),sQuery(id+"F0.wireOp",EDGE,"E0.left"),sQuery(id+"F0.wireOp",EDGE,"E0.right")])],"isStart":true}),makeQuery(id+"F5.opExtrude","CAP_FACE",FACE,{"disambiguationData":[OSD([sQuery(id+"F4.wireOp",EDGE,"E4"),sQuery(id+"F4.wireOp",EDGE,"E5"),sQuery(id+"F4.wireOp",EDGE,"E6")])],"isStart":true}),makeQuery(id+"F5.opExtrude","CAP_FACE",FACE,{"disambiguationData":[OSD([sQuery(id+"F4.wireOp",EDGE,"E7"),sQuery(id+"F4.wireOp",EDGE,"E8"),sQuery(id+"F4.wireOp",EDGE,"E9")])],"isStart":true})]}),makeQuery(id+"F7.opExtrude","CAP_FACE",FACE,{"disambiguationData":[OSD([sQuery(id+"F6.wireOp",EDGE,"E10.bottom"),sQuery(id+"F6.wireOp",EDGE,"E10.top"),sQuery(id+"F6.wireOp",EDGE,"E10.left"),sQuery(id+"F6.wireOp",EDGE,"E10.right"),sQuery(id+"F6.wireOp",EDGE,"E14.filletArc"),sQuery(id+"F6.wireOp",EDGE,"E15.filletArc")])],"isStart":true}),makeQuery(id+"F7.opExtrude","CAP_FACE",FACE,{"disambiguationData":[OSD([sQuery(id+"F6.wireOp",EDGE,"E11.bottom"),sQuery(id+"F6.wireOp",EDGE,"E11.top"),sQuery(id+"F6.wireOp",EDGE,"E11.left"),sQuery(id+"F6.wireOp",EDGE,"E11.right"),sQuery(id+"F6.wireOp",EDGE,"E12.filletArc"),sQuery(id+"F6.wireOp",EDGE,"E13.filletArc")])],"isStart":true})]}),makeQuery(id+"F11.opExtrude","SWEPT_FACE",FACE,{"disambiguationData":[OSD([sQuery(id+"F10.wireOp",EDGE,"E18.top")])]})]}),makeQuery(id+"F13.opExtrude","CAP_FACE",FACE,{"disambiguationData":[OSD([sQuery(id+"F12.wireOp",EDGE,"E19.bottom"),sQuery(id+"F12.wireOp",EDGE,"E19.top"),sQuery(id+"F12.wireOp",EDGE,"E19.left"),sQuery(id+"F12.wireOp",EDGE,"E19.right")])],"isStart":true})]}),makeQuery(id+"F15.opExtrude","SWEPT_FACE",FACE,{"disambiguationData":[OSD([sQuery(id+"F14.wireOp",EDGE,"E20.top")])]}),makeQuery(id+"F15.opExtrude","SWEPT_FACE",FACE,{"disambiguationData":[OSD([sQuery(id+"F14.wireOp",EDGE,"E21.bottom")])]})]}),makeQuery(id+"F23.opExtrude","CAP_FACE",FACE,{"disambiguationData":[OSD([sQuery(id+"F22.wireOp",EDGE,"E27")])],"isStart":false})]}),makeQuery(id+"F25.opExtrude","CAP_FACE",FACE,{"disambiguationData":[OSD([sQuery(id+"F24.wireOp",EDGE,"E28")])],"isStart":false})]});
            var sketch = newSketch(context, id + "F43", { "sketchPlane" : qUnion([Q0])});
            skLineSegment(sketch, "E37", {"start": v(7, 0.33) * mm, "end": v(10.73, -3) * mm});
            skLineSegment(sketch, "E38", {"start": v(10.73, -3) * mm, "end": v(7, -3) * mm});
            skLineSegment(sketch, "E39", {"start": v(7, -3) * mm, "end": v(7, 0.33) * mm});
            skLineSegment(sketch, "E40", {"start": v(0, 0.33) * mm, "end": v(-3.73, -3) * mm});
            skLineSegment(sketch, "E41", {"start": v(-3.73, -3) * mm, "end": v(0, -3) * mm});
            skLineSegment(sketch, "E42", {"start": v(0, -3) * mm, "end": v(0, 0.33) * mm});
            skSolve(sketch);
        }
        {
            var Q0;
            Q0 = qSketchRegion(id + "F43", true);
            var Q1;
            {var subQ0=sQuery(id+"F12.wireOp",EDGE,"E19.top");var subQ5=makeQuery(id+"F1.opExtrude","SWEPT_FACE",FACE,{"disambiguationData":[OSD([sQuery(id+"F0.wireOp",EDGE,"E0.left")])]});var subQ8=sQuery(id+"F6.wireOp",EDGE,"E10.bottom");var subQ9=sQuery(id+"F12.wireOp",EDGE,"E19.bottom");var subQ10=sQuery(id+"F12.wireOp",EDGE,"E19.left");Q1=makeQuery(id+"F31.boolean.opBoolean","SPLIT",FACE,{"disambiguationData":[TD([subQ5])],"derivedFrom":makeQuery(id+"F15.boolean.opBoolean","MERGE",FACE,{"derivedFrom":[makeQuery(id+"F7.opExtrude","CAP_FACE",FACE,{"disambiguationData":[OSD([subQ8,sQuery(id+"F6.wireOp",EDGE,"E10.top"),sQuery(id+"F6.wireOp",EDGE,"E10.left"),sQuery(id+"F6.wireOp",EDGE,"E10.right"),sQuery(id+"F6.wireOp",EDGE,"E14.filletArc"),sQuery(id+"F6.wireOp",EDGE,"E15.filletArc")])],"isStart":false}),makeQuery(id+"F13.boolean.opBoolean","SPLIT",FACE,{"disambiguationData":[TD([subQ5])],"derivedFrom":makeQuery(id+"F13.opExtrude","CAP_FACE",FACE,{"disambiguationData":[OSD([subQ9,subQ0,subQ10,sQuery(id+"F12.wireOp",EDGE,"E19.right")])],"isStart":false})}),makeQuery(id+"F15.opExtrude","SWEPT_FACE",FACE,{"disambiguationData":[OSD([sQuery(id+"F14.wireOp",EDGE,"E21.top")])]})]})});}
            extrude(context, id + "F44", {"entities" : qUnion([Q0]), "operationType" : NewBodyOperationType.ADD, "endBound" : BoundingType.UP_TO_SURFACE, "oppositeDirection" : true, "endBoundEntityFace" : qUnion([Q1]), "depth" : 25 * mm});
        }
    });
